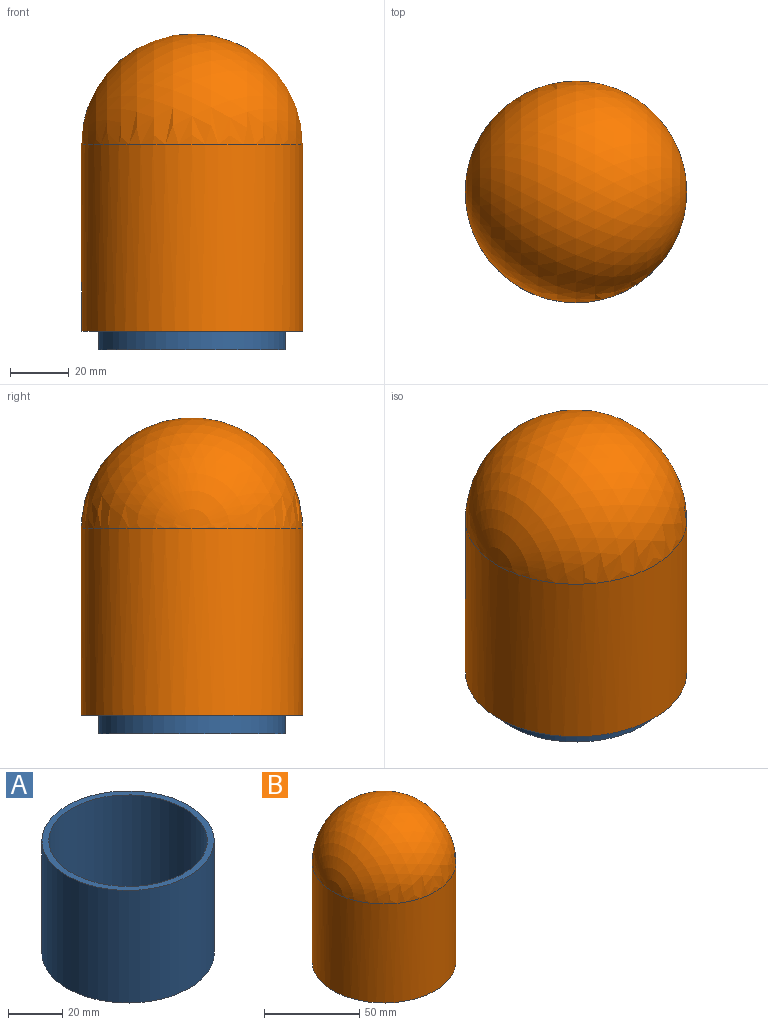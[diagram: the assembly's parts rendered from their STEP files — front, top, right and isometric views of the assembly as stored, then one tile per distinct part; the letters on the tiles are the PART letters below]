
ASSEMBLY  parts=2 mates=1
PART A: 6 faces, bbox 63.5x63.5x50.8 mm
  f0: cylinder r=31.75mm len=63.5mm, axis (0,0,-1), area 10134.1mm2, adj f1,f2
  f1: plane 63.5x63.5mm, normal (0,0,1), area 486.4mm2, adj f0,f3
  f2: plane 63.5x63.5mm, normal (0,0,-1), area 2756.5mm2, adj f0,f5
  f3: cylinder r=29.21mm len=58.42mm, axis (0,0,-1), area 8857.2mm2, adj f1,f4
  f4: plane 58.42x58.42mm, normal (0,0,1), area 2270mm2, adj f3,f5
  f5: cylinder r=11.43mm len=22.86mm, axis (0,0,-1), area 182.4mm2, adj f2,f4
PART B: 5 faces, bbox 75.2x75.2x101.1 mm
  f0: cylinder r=37.62mm len=75.24mm, axis (0,0,-1), area 15009.8mm2, adj f1,f2
  f1: plane 75.24x75.24mm, normal (0,0,-1), area 580.1mm2, adj f0,f3
  f2: sphere r=37.62mm, area 8892.5mm2, adj f0
  f3: cylinder r=35.08mm len=70.16mm, axis (0,0,-1), area 13996.4mm2, adj f1,f4
  f4: sphere r=35.08mm, area 7732.3mm2, adj f3
PLACE A t=(0,0,-50.8)mm
PLACE B t=(0,0,-44.45)mm
MATE cylindrical A.f5 <-> B.f0  axis (0,0,-1) through (0,0,-50.8)mm
